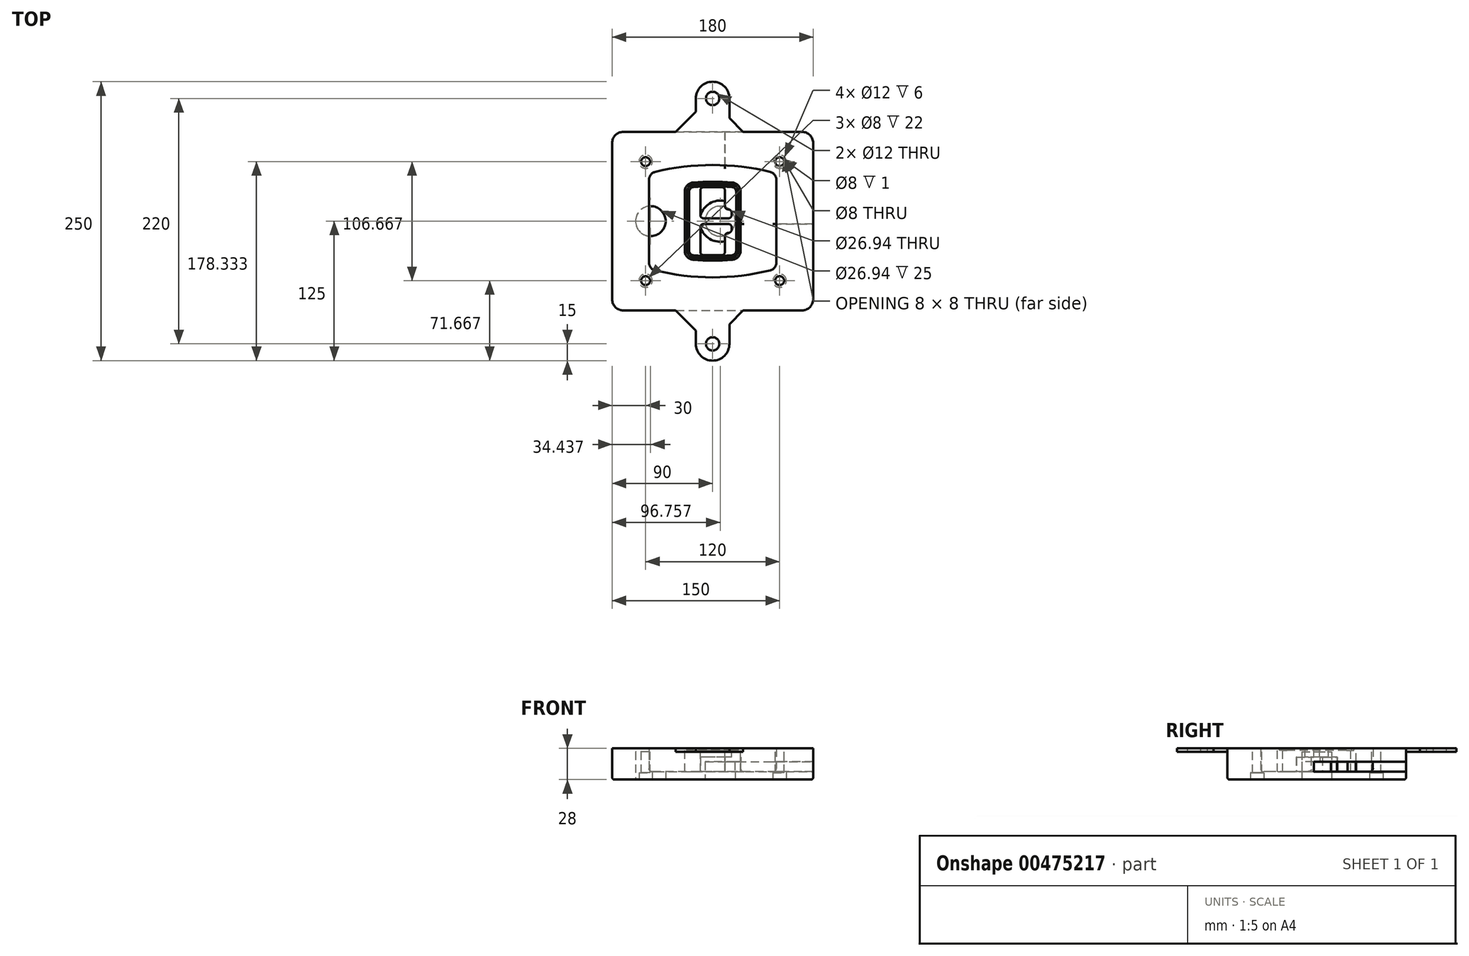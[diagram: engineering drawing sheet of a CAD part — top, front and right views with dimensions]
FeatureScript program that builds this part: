
annotation { "Feature Type Name" : "Feature", "Feature Type Description" : "" }
export const myFeature = defineFeature(function(context is Context, id is Id, definition is map)
    precondition{}
    {
        {
            var Q0;
            Q0=qCreatedBy(makeId("Top.planeOp"),FACE);
            var sketch = newSketch(context, id + "F0", { "sketchPlane" : qUnion([Q0])});
            skPoint(sketch, "E0.rect.middle", {"position": v(0, 0) * mm});
            skLineSegment(sketch, "E1.bottom", {"start": v(-80, -80) * mm, "end": v(80, -80) * mm});
            skLineSegment(sketch, "E1.top", {"start": v(-80, 80) * mm, "end": v(80, 80) * mm});
            skLineSegment(sketch, "E1.left", {"start": v(-90, -70) * mm, "end": v(-90, 70) * mm});
            skLineSegment(sketch, "E1.right", {"start": v(90, -70) * mm, "end": v(90, 70) * mm});
            skLineSegment(sketch, "E2", {"start": v(-90, 80) * mm, "end": v(90, -80) * mm, "construction": true});
            skLineSegment(sketch, "E3", {"start": v(90, 80) * mm, "end": v(-90, -80) * mm, "construction": true});
            skCircle(sketch, "E4", {"center": v(-60, 53.33) * mm, "radius": 4 * mm});
            skCircle(sketch, "E5", {"center": v(60, 53.33) * mm, "radius": 4 * mm});
            skCircle(sketch, "E6", {"center": v(60, -53.33) * mm, "radius": 4 * mm});
            skCircle(sketch, "E7", {"center": v(-60, -53.33) * mm, "radius": 4 * mm});
            skLineSegment(sketch, "E8", {"start": v(-60, 53.33) * mm, "end": v(60, 53.33) * mm, "construction": true});
            skLineSegment(sketch, "E9", {"start": v(60, 53.33) * mm, "end": v(60, -53.33) * mm, "construction": true});
            skLineSegment(sketch, "E10", {"start": v(60, -53.33) * mm, "end": v(-60, -53.33) * mm, "construction": true});
            skLineSegment(sketch, "E11", {"start": v(-60, -53.33) * mm, "end": v(-60, 53.33) * mm, "construction": true});
            skLineSegment(sketch, "E12", {"start": v(-60, 37.3) * mm, "end": v(-60, -37.3) * mm});
            skLineSegment(sketch, "E13", {"start": v(60, 37.3) * mm, "end": v(60, -37.3) * mm});
            skArc(sketch, "E14", {"start": v(52.38, 47.01) * mm, "mid": v(0, 53.33) * mm, "end": v(-52.38, 47.01) * mm});
            skArc(sketch, "E15", {"start": v(-52.38, -47.01) * mm, "mid": v(0, -53.33) * mm, "end": v(52.38, -47.01) * mm});
            skLineSegment(sketch, "E16", {"start": v(-60, 0) * mm, "end": v(60, 0) * mm, "construction": true});
            skPoint(sketch, "E17.visualSharp", {"position": v(-60, -45) * mm});
            skArc(sketch, "E17.filletArc", {"start": v(-60, -37.3) * mm, "mid": v(-57.87, -43.47) * mm, "end": v(-52.38, -47.01) * mm});
            skPoint(sketch, "E18.visualSharp", {"position": v(-60, 45) * mm});
            skArc(sketch, "E18.filletArc", {"start": v(-52.38, 47.01) * mm, "mid": v(-57.87, 43.47) * mm, "end": v(-60, 37.3) * mm});
            skPoint(sketch, "E19.visualSharp", {"position": v(60, 45) * mm});
            skArc(sketch, "E19.filletArc", {"start": v(60, 37.3) * mm, "mid": v(57.87, 43.47) * mm, "end": v(52.38, 47.01) * mm});
            skPoint(sketch, "E20.visualSharp", {"position": v(60, -45) * mm});
            skArc(sketch, "E20.filletArc", {"start": v(52.38, -47.01) * mm, "mid": v(57.87, -43.47) * mm, "end": v(60, -37.3) * mm});
            skPoint(sketch, "E21.visualSharp", {"position": v(-90, 80) * mm});
            skArc(sketch, "E21.filletArc", {"start": v(-80, 80) * mm, "mid": v(-87.07, 77.07) * mm, "end": v(-90, 70) * mm});
            skPoint(sketch, "E22.visualSharp", {"position": v(90, 80) * mm});
            skArc(sketch, "E22.filletArc", {"start": v(90, 70) * mm, "mid": v(87.07, 77.07) * mm, "end": v(80, 80) * mm});
            skPoint(sketch, "E23.visualSharp", {"position": v(90, -80) * mm});
            skArc(sketch, "E23.filletArc", {"start": v(80, -80) * mm, "mid": v(87.07, -77.07) * mm, "end": v(90, -70) * mm});
            skPoint(sketch, "E24.visualSharp", {"position": v(-90, -80) * mm});
            skArc(sketch, "E24.filletArc", {"start": v(-90, -70) * mm, "mid": v(-87.07, -77.07) * mm, "end": v(-80, -80) * mm});
            skArc(sketch, "E25.0", {"start": v(57, 37.3) * mm, "mid": v(55.5, 41.62) * mm, "end": v(51.67, 44.1) * mm});
            skLineSegment(sketch, "E25.1", {"start": v(57, 37.3) * mm, "end": v(57, -37.3) * mm});
            skArc(sketch, "E25.2", {"start": v(51.67, -44.1) * mm, "mid": v(55.5, -41.62) * mm, "end": v(57, -37.3) * mm});
            skArc(sketch, "E25.3", {"start": v(-51.67, -44.1) * mm, "mid": v(0, -50.33) * mm, "end": v(51.67, -44.1) * mm});
            skArc(sketch, "E25.4", {"start": v(-57, -37.3) * mm, "mid": v(-55.5, -41.62) * mm, "end": v(-51.67, -44.1) * mm});
            skArc(sketch, "E25.5", {"start": v(51.67, 44.1) * mm, "mid": v(0, 50.33) * mm, "end": v(-51.67, 44.1) * mm});
            skLineSegment(sketch, "E25.6", {"start": v(-57, 37.3) * mm, "end": v(-57, -37.3) * mm});
            skArc(sketch, "E25.7", {"start": v(-51.67, 44.1) * mm, "mid": v(-55.5, 41.62) * mm, "end": v(-57, 37.3) * mm});
            skArc(sketch, "E26.0", {"start": v(-53.33, 50.9) * mm, "mid": v(-61.01, 45.94) * mm, "end": v(-64, 37.3) * mm});
            skArc(sketch, "E26.1", {"start": v(53.33, 50.9) * mm, "mid": v(0, 57.33) * mm, "end": v(-53.33, 50.9) * mm});
            skArc(sketch, "E26.2", {"start": v(64, 37.3) * mm, "mid": v(61.01, 45.94) * mm, "end": v(53.33, 50.9) * mm});
            skLineSegment(sketch, "E26.3", {"start": v(64, 37.3) * mm, "end": v(64, -37.3) * mm});
            skArc(sketch, "E26.4", {"start": v(53.33, -50.9) * mm, "mid": v(61.01, -45.94) * mm, "end": v(64, -37.3) * mm});
            skLineSegment(sketch, "E26.5", {"start": v(-64, 37.3) * mm, "end": v(-64, -37.3) * mm});
            skArc(sketch, "E26.6", {"start": v(-53.33, -50.9) * mm, "mid": v(0, -57.33) * mm, "end": v(53.33, -50.9) * mm});
            skArc(sketch, "E26.7", {"start": v(-64, -37.3) * mm, "mid": v(-61.01, -45.94) * mm, "end": v(-53.33, -50.9) * mm});
            skSolve(sketch);
        }
        {
            var Q0;
            Q0=makeQuery(id+"F0.imprint","IMPRINT",FACE,{"disambiguationData":[TD([[makeQuery(id+"F0.imprint","IMPRINT",EDGE,{"derivedFrom":sQuery(id+"F0.wireOp",EDGE,"E1.bottom")}),1.0]])]});
            var Q1;
            Q1=makeQuery(id+"F0.imprint","IMPRINT",FACE,{"disambiguationData":[TD([[makeQuery(id+"F0.imprint","IMPRINT",EDGE,{"derivedFrom":sQuery(id+"F0.wireOp",EDGE,"E12")}),1.0]])]});
            var Q2;
            Q2=makeQuery(id+"F0.imprint","IMPRINT",FACE,{"disambiguationData":[TD([[makeQuery(id+"F0.imprint","IMPRINT",EDGE,{"derivedFrom":sQuery(id+"F0.wireOp",EDGE,"E25.0")}),1.0]])]});
            var Q3;
            Q3=makeQuery(id+"F0.imprint","IMPRINT",FACE,{"disambiguationData":[TD([[makeQuery(id+"F0.imprint","IMPRINT",EDGE,{"derivedFrom":sQuery(id+"F0.wireOp",EDGE,"E12")}),-1.0]])]});
            extrude(context, id + "F1", {"entities" : qUnion([Q0, Q1, Q2, Q3]), "oppositeDirection" : true, "depth" : 25 * mm});
        }
        {
            var Q0;
            Q0=makeQuery(id+"F0.imprint","IMPRINT",FACE,{"disambiguationData":[TD([[makeQuery(id+"F0.imprint","IMPRINT",EDGE,{"derivedFrom":sQuery(id+"F0.wireOp",EDGE,"E12")}),1.0]])]});
            extrude(context, id + "F2", {"entities" : qUnion([Q0]), "operationType" : NewBodyOperationType.ADD, "depth" : 3 * mm});
        }
        {
            var Q0;
            Q0=makeQuery(id+"F0.imprint","IMPRINT",FACE,{"disambiguationData":[TD([[makeQuery(id+"F0.imprint","IMPRINT",EDGE,{"derivedFrom":sQuery(id+"F0.wireOp",EDGE,"E25.0")}),1.0]])]});
            extrude(context, id + "F3", {"entities" : qUnion([Q0]), "operationType" : NewBodyOperationType.REMOVE, "oppositeDirection" : true, "depth" : 18 * mm});
        }
        {
            var Q0;
            Q0=makeQuery(id+"F2.opExtrude","CAP_FACE",FACE,{"disambiguationData":[OSD([sQuery(id+"F0.wireOp",EDGE,"E12"),sQuery(id+"F0.wireOp",EDGE,"E13"),sQuery(id+"F0.wireOp",EDGE,"E14"),sQuery(id+"F0.wireOp",EDGE,"E15"),sQuery(id+"F0.wireOp",EDGE,"E17.filletArc"),sQuery(id+"F0.wireOp",EDGE,"E18.filletArc"),sQuery(id+"F0.wireOp",EDGE,"E19.filletArc"),sQuery(id+"F0.wireOp",EDGE,"E20.filletArc"),sQuery(id+"F0.wireOp",EDGE,"E25.0"),sQuery(id+"F0.wireOp",EDGE,"E25.1"),sQuery(id+"F0.wireOp",EDGE,"E25.2"),sQuery(id+"F0.wireOp",EDGE,"E25.3"),sQuery(id+"F0.wireOp",EDGE,"E25.4"),sQuery(id+"F0.wireOp",EDGE,"E25.5"),sQuery(id+"F0.wireOp",EDGE,"E25.6"),sQuery(id+"F0.wireOp",EDGE,"E25.7")])],"isStart":false});
            var sketch = newSketch(context, id + "F4", { "sketchPlane" : qUnion([Q0])});
            skArc(sketch, "E27.0", {"start": v(-17.7, -34.56) * mm, "mid": v(0, -35.33) * mm, "end": v(17.7, -34.56) * mm});
            skArc(sketch, "E28.0", {"start": v(17.7, 34.56) * mm, "mid": v(0, 35.33) * mm, "end": v(-17.7, 34.56) * mm});
            skLineSegment(sketch, "E29", {"start": v(-25, 26.59) * mm, "end": v(-25, -26.59) * mm});
            skLineSegment(sketch, "E30", {"start": v(25, 26.59) * mm, "end": v(25, -26.59) * mm});
            skLineSegment(sketch, "E31", {"start": v(-25, 33.78) * mm, "end": v(25, 33.78) * mm, "construction": true});
            skLineSegment(sketch, "E32", {"start": v(-25, -33.78) * mm, "end": v(25, -33.78) * mm, "construction": true});
            skPoint(sketch, "E33.visualSharp", {"position": v(-25, 33.78) * mm});
            skArc(sketch, "E33.filletArc", {"start": v(-17.7, 34.56) * mm, "mid": v(-22.9, 32) * mm, "end": v(-25, 26.59) * mm});
            skPoint(sketch, "E34.visualSharp", {"position": v(25, 33.78) * mm});
            skArc(sketch, "E34.filletArc", {"start": v(25, 26.59) * mm, "mid": v(22.9, 32) * mm, "end": v(17.7, 34.56) * mm});
            skPoint(sketch, "E35.visualSharp", {"position": v(25, -33.78) * mm});
            skArc(sketch, "E35.filletArc", {"start": v(17.7, -34.56) * mm, "mid": v(22.9, -32) * mm, "end": v(25, -26.59) * mm});
            skPoint(sketch, "E36.visualSharp", {"position": v(-25, -33.78) * mm});
            skArc(sketch, "E36.filletArc", {"start": v(-25, -26.59) * mm, "mid": v(-22.9, -32) * mm, "end": v(-17.7, -34.56) * mm});
            skArc(sketch, "E37.0", {"start": v(51.67, 44.1) * mm, "mid": v(0, 50.33) * mm, "end": v(-51.67, 44.1) * mm});
            skArc(sketch, "E37.1", {"start": v(-51.67, 44.1) * mm, "mid": v(-55.5, 41.62) * mm, "end": v(-57, 37.3) * mm});
            skLineSegment(sketch, "E37.2", {"start": v(-57, 37.3) * mm, "end": v(-57, -37.3) * mm});
            skArc(sketch, "E37.3", {"start": v(-57, -37.3) * mm, "mid": v(-55.5, -41.62) * mm, "end": v(-51.67, -44.1) * mm});
            skArc(sketch, "E37.4", {"start": v(-51.67, -44.1) * mm, "mid": v(0, -50.33) * mm, "end": v(51.67, -44.1) * mm});
            skArc(sketch, "E37.5", {"start": v(51.67, -44.1) * mm, "mid": v(55.5, -41.62) * mm, "end": v(57, -37.3) * mm});
            skLineSegment(sketch, "E37.6", {"start": v(57, 37.3) * mm, "end": v(57, -37.3) * mm});
            skArc(sketch, "E37.7", {"start": v(57, 37.3) * mm, "mid": v(55.5, 41.62) * mm, "end": v(51.67, 44.1) * mm});
            skLineSegment(sketch, "E38.0", {"start": v(23, 26.59) * mm, "end": v(23, -26.59) * mm});
            skArc(sketch, "E38.1", {"start": v(17.53, -32.56) * mm, "mid": v(21.42, -30.64) * mm, "end": v(23, -26.59) * mm});
            skArc(sketch, "E38.2", {"start": v(-17.53, -32.56) * mm, "mid": v(0, -33.33) * mm, "end": v(17.53, -32.56) * mm});
            skArc(sketch, "E38.3", {"start": v(-23, -26.59) * mm, "mid": v(-21.42, -30.64) * mm, "end": v(-17.53, -32.56) * mm});
            skLineSegment(sketch, "E38.4", {"start": v(-23, 26.59) * mm, "end": v(-23, -26.59) * mm});
            skArc(sketch, "E38.5", {"start": v(23, 26.59) * mm, "mid": v(21.42, 30.64) * mm, "end": v(17.53, 32.56) * mm});
            skArc(sketch, "E38.6", {"start": v(-17.53, 32.56) * mm, "mid": v(-21.42, 30.64) * mm, "end": v(-23, 26.59) * mm});
            skArc(sketch, "E38.7", {"start": v(17.53, 32.56) * mm, "mid": v(0, 33.33) * mm, "end": v(-17.53, 32.56) * mm});
            skArc(sketch, "E39.0", {"start": v(21, 26.59) * mm, "mid": v(19.95, 29.29) * mm, "end": v(17.35, 30.57) * mm});
            skLineSegment(sketch, "E39.1", {"start": v(21, 26.59) * mm, "end": v(21, -26.59) * mm});
            skArc(sketch, "E39.2", {"start": v(17.35, -30.57) * mm, "mid": v(19.95, -29.29) * mm, "end": v(21, -26.59) * mm});
            skArc(sketch, "E39.3", {"start": v(-17.35, -30.57) * mm, "mid": v(0, -31.33) * mm, "end": v(17.35, -30.57) * mm});
            skArc(sketch, "E39.4", {"start": v(-21, -26.59) * mm, "mid": v(-19.95, -29.29) * mm, "end": v(-17.35, -30.57) * mm});
            skArc(sketch, "E39.5", {"start": v(17.35, 30.57) * mm, "mid": v(0, 31.33) * mm, "end": v(-17.35, 30.57) * mm});
            skLineSegment(sketch, "E39.6", {"start": v(-21, 26.59) * mm, "end": v(-21, -26.59) * mm});
            skArc(sketch, "E39.7", {"start": v(-17.35, 30.57) * mm, "mid": v(-19.95, 29.29) * mm, "end": v(-21, 26.59) * mm});
            skLineSegment(sketch, "E40", {"start": v(-25, 0) * mm, "end": v(25, 0) * mm, "construction": true});
            skLineSegment(sketch, "E41", {"start": v(-11, 5.5) * mm, "end": v(-11, 27.5) * mm});
            skLineSegment(sketch, "E42", {"start": v(-8, 30.5) * mm, "end": v(8, 30.5) * mm});
            skLineSegment(sketch, "E43", {"start": v(11, 27.5) * mm, "end": v(11, 13.5) * mm});
            skLineSegment(sketch, "E44", {"start": v(14, 10.5) * mm, "end": v(14, 10.5) * mm});
            skLineSegment(sketch, "E45", {"start": v(17, 7.5) * mm, "end": v(17, 5.5) * mm});
            skLineSegment(sketch, "E46", {"start": v(14, 2.5) * mm, "end": v(-8, 2.5) * mm});
            skPoint(sketch, "E47.visualSharp", {"position": v(-11, 30.5) * mm});
            skArc(sketch, "E47.filletArc", {"start": v(-8, 30.5) * mm, "mid": v(-10.12, 29.62) * mm, "end": v(-11, 27.5) * mm});
            skPoint(sketch, "E48.visualSharp", {"position": v(11, 30.5) * mm});
            skArc(sketch, "E48.filletArc", {"start": v(11, 27.5) * mm, "mid": v(10.12, 29.62) * mm, "end": v(8, 30.5) * mm});
            skPoint(sketch, "E49.visualSharp", {"position": v(11, 10.5) * mm});
            skArc(sketch, "E49.filletArc", {"start": v(11, 13.5) * mm, "mid": v(11.88, 11.38) * mm, "end": v(14, 10.5) * mm});
            skPoint(sketch, "E50.visualSharp", {"position": v(17, 10.5) * mm});
            skArc(sketch, "E50.filletArc", {"start": v(17, 7.5) * mm, "mid": v(16.12, 9.62) * mm, "end": v(14, 10.5) * mm});
            skPoint(sketch, "E51.visualSharp", {"position": v(17, 2.5) * mm});
            skArc(sketch, "E51.filletArc", {"start": v(14, 2.5) * mm, "mid": v(16.12, 3.38) * mm, "end": v(17, 5.5) * mm});
            skPoint(sketch, "E52.visualSharp", {"position": v(-11, 2.5) * mm});
            skArc(sketch, "E52.filletArc", {"start": v(-11, 5.5) * mm, "mid": v(-10.12, 3.38) * mm, "end": v(-8, 2.5) * mm});
            skLineSegment(sketch, "E53.0.MirrorCS", {"start": v(14, -2.5) * mm, "end": v(-8, -2.5) * mm});
            skArc(sketch, "E54.0.MirrorCS", {"start": v(-11, -5.5) * mm, "mid": v(-10.12, -3.38) * mm, "end": v(-8, -2.5) * mm});
            skLineSegment(sketch, "E55.0.MirrorCS", {"start": v(-11, -5.5) * mm, "end": v(-11, -27.5) * mm});
            skArc(sketch, "E56.0.MirrorCS", {"start": v(-8, -30.5) * mm, "mid": v(-10.12, -29.62) * mm, "end": v(-11, -27.5) * mm});
            skLineSegment(sketch, "E57.0.MirrorCS", {"start": v(-8, -30.5) * mm, "end": v(8, -30.5) * mm});
            skArc(sketch, "E58.0.MirrorCS", {"start": v(11, -27.5) * mm, "mid": v(10.12, -29.62) * mm, "end": v(8, -30.5) * mm});
            skLineSegment(sketch, "E59.0.MirrorCS", {"start": v(11, -27.5) * mm, "end": v(11, -13.5) * mm});
            skArc(sketch, "E60.0.MirrorCS", {"start": v(11, -13.5) * mm, "mid": v(11.88, -11.38) * mm, "end": v(14, -10.5) * mm});
            skArc(sketch, "E61.0.MirrorCS", {"start": v(17, -7.5) * mm, "mid": v(16.12, -9.62) * mm, "end": v(14, -10.5) * mm});
            skLineSegment(sketch, "E62.0.MirrorCS", {"start": v(17, -7.5) * mm, "end": v(17, -5.5) * mm});
            skArc(sketch, "E63.0.MirrorCS", {"start": v(14, -2.5) * mm, "mid": v(16.12, -3.38) * mm, "end": v(17, -5.5) * mm});
            skSolve(sketch);
        }
        {
            var Q0;
            Q0=makeQuery(id+"F4.imprint","IMPRINT",FACE,{"disambiguationData":[TD([[makeQuery(id+"F4.imprint","IMPRINT",EDGE,{"derivedFrom":sQuery(id+"F4.wireOp",EDGE,"E27.0")}),1.0]])]});
            var Q1;
            Q1=makeQuery(id+"F4.imprint","IMPRINT",FACE,{"disambiguationData":[TD([[makeQuery(id+"F4.imprint","IMPRINT",EDGE,{"derivedFrom":sQuery(id+"F4.wireOp",EDGE,"E38.0")}),-1.0]])]});
            var Q2;
            Q2=makeQuery(id+"F4.imprint","IMPRINT",FACE,{"disambiguationData":[TD([[makeQuery(id+"F4.imprint","IMPRINT",EDGE,{"derivedFrom":sQuery(id+"F4.wireOp",EDGE,"E39.0")}),1.0]])]});
            extrude(context, id + "F5", {"entities" : qUnion([Q0, Q1, Q2]), "operationType" : NewBodyOperationType.ADD, "endBound" : BoundingType.UP_TO_NEXT, "oppositeDirection" : true, "depth" : 25 * mm});
        }
        {
            var Q0;
            Q0=makeQuery(id+"F4.imprint","IMPRINT",FACE,{"disambiguationData":[TD([[makeQuery(id+"F4.imprint","IMPRINT",EDGE,{"derivedFrom":sQuery(id+"F4.wireOp",EDGE,"E38.0")}),-1.0]])]});
            extrude(context, id + "F6", {"entities" : qUnion([Q0]), "operationType" : NewBodyOperationType.REMOVE, "oppositeDirection" : true, "depth" : 2 * mm});
        }
        {
            var Q0;
            Q0=makeQuery(id+"F1.opExtrude","CAP_FACE",FACE,{"disambiguationData":[OSD([sQuery(id+"F0.wireOp",EDGE,"E1.bottom"),sQuery(id+"F0.wireOp",EDGE,"E1.top"),sQuery(id+"F0.wireOp",EDGE,"E1.left"),sQuery(id+"F0.wireOp",EDGE,"E1.right"),sQuery(id+"F0.wireOp",EDGE,"E4"),sQuery(id+"F0.wireOp",EDGE,"E5"),sQuery(id+"F0.wireOp",EDGE,"E6"),sQuery(id+"F0.wireOp",EDGE,"E7"),sQuery(id+"F0.wireOp",EDGE,"E21.filletArc"),sQuery(id+"F0.wireOp",EDGE,"E22.filletArc"),sQuery(id+"F0.wireOp",EDGE,"E23.filletArc"),sQuery(id+"F0.wireOp",EDGE,"E24.filletArc")])],"isStart":false});
            var sketch = newSketch(context, id + "F7", { "sketchPlane" : qUnion([Q0])});
            skCircle(sketch, "E64", {"center": v(6.76, 0) * mm, "radius": 13.47 * mm});
            skCircle(sketch, "E65", {"center": v(-55.56, 0) * mm, "radius": 13.47 * mm});
            skLineSegment(sketch, "E66", {"start": v(90, 0) * mm, "end": v(-90, 0) * mm});
            skCircle(sketch, "E67", {"center": v(6.76, 0) * mm, "radius": 18.47 * mm});
            skCircle(sketch, "E68", {"center": v(60, -53.33) * mm, "radius": 6 * mm});
            skCircle(sketch, "E69", {"center": v(-60, -53.33) * mm, "radius": 6 * mm});
            skCircle(sketch, "E70", {"center": v(-60, 53.33) * mm, "radius": 6 * mm});
            skCircle(sketch, "E71", {"center": v(60, 53.33) * mm, "radius": 6 * mm});
            skSolve(sketch);
        }
        {
            var Q0;
            {var subQ1=sQuery(id+"F7.wireOp",EDGE,"E66");var subQ4=sQuery(id+"F7.wireOp",EDGE,"E64");var subQ6=makeQuery(id+"F7.imprint","INTERSECT",VERTEX,{"disambiguationData":[OD(0.0)],"derivedFrom":[subQ4,subQ1]});Q0=makeQuery(id+"F7.imprint","IMPRINT",FACE,{"disambiguationData":[TD([[makeQuery(id+"F7.imprint","IMPRINT",EDGE,{"disambiguationData":[TD([[subQ6,-1.0]])],"derivedFrom":subQ4}),-1.0]])]});}
            var Q1;
            {var subQ0=sQuery(id+"F7.wireOp",EDGE,"E66");var subQ1=sQuery(id+"F7.wireOp",EDGE,"E64");var subQ3=makeQuery(id+"F7.imprint","INTERSECT",VERTEX,{"disambiguationData":[OD(0.0)],"derivedFrom":[subQ1,subQ0]});Q1=makeQuery(id+"F7.imprint","IMPRINT",FACE,{"disambiguationData":[TD([[makeQuery(id+"F7.imprint","IMPRINT",EDGE,{"disambiguationData":[TD([[subQ3,-1.0]])],"derivedFrom":subQ1}),1.0]])]});}
            var Q2;
            {var subQ0=sQuery(id+"F7.wireOp",EDGE,"E66");var subQ1=sQuery(id+"F7.wireOp",EDGE,"E64");var subQ3=makeQuery(id+"F7.imprint","INTERSECT",VERTEX,{"disambiguationData":[OD(0.0)],"derivedFrom":[subQ1,subQ0]});Q2=makeQuery(id+"F7.imprint","IMPRINT",FACE,{"disambiguationData":[TD([[makeQuery(id+"F7.imprint","IMPRINT",EDGE,{"disambiguationData":[TD([[subQ3,1.0]])],"derivedFrom":subQ1}),1.0]])]});}
            var Q3;
            {var subQ1=sQuery(id+"F7.wireOp",EDGE,"E66");var subQ4=sQuery(id+"F7.wireOp",EDGE,"E64");var subQ6=makeQuery(id+"F7.imprint","INTERSECT",VERTEX,{"disambiguationData":[OD(0.0)],"derivedFrom":[subQ4,subQ1]});Q3=makeQuery(id+"F7.imprint","IMPRINT",FACE,{"disambiguationData":[TD([[makeQuery(id+"F7.imprint","IMPRINT",EDGE,{"disambiguationData":[TD([[subQ6,1.0]])],"derivedFrom":subQ4}),-1.0]])]});}
            extrude(context, id + "F8", {"entities" : qUnion([Q0, Q1, Q2, Q3]), "operationType" : NewBodyOperationType.ADD, "oppositeDirection" : true, "depth" : 20 * mm});
        }
        {
            var Q0;
            {var subQ0=sQuery(id+"F7.wireOp",EDGE,"E66");var subQ1=sQuery(id+"F7.wireOp",EDGE,"E64");var subQ3=makeQuery(id+"F7.imprint","INTERSECT",VERTEX,{"disambiguationData":[OD(0.0)],"derivedFrom":[subQ1,subQ0]});Q0=makeQuery(id+"F7.imprint","IMPRINT",FACE,{"disambiguationData":[TD([[makeQuery(id+"F7.imprint","IMPRINT",EDGE,{"disambiguationData":[TD([[subQ3,-1.0]])],"derivedFrom":subQ1}),1.0]])]});}
            var Q1;
            {var subQ0=sQuery(id+"F7.wireOp",EDGE,"E66");var subQ1=sQuery(id+"F7.wireOp",EDGE,"E64");var subQ3=makeQuery(id+"F7.imprint","INTERSECT",VERTEX,{"disambiguationData":[OD(0.0)],"derivedFrom":[subQ1,subQ0]});Q1=makeQuery(id+"F7.imprint","IMPRINT",FACE,{"disambiguationData":[TD([[makeQuery(id+"F7.imprint","IMPRINT",EDGE,{"disambiguationData":[TD([[subQ3,1.0]])],"derivedFrom":subQ1}),1.0]])]});}
            extrude(context, id + "F9", {"entities" : qUnion([Q0, Q1]), "operationType" : NewBodyOperationType.REMOVE, "oppositeDirection" : true, "depth" : 16 * mm});
        }
        {
            var Q0;
            {var subQ0=sQuery(id+"F7.wireOp",EDGE,"E66");var subQ1=sQuery(id+"F7.wireOp",EDGE,"E65");var subQ3=makeQuery(id+"F7.imprint","INTERSECT",VERTEX,{"disambiguationData":[OD(0.0)],"derivedFrom":[subQ1,subQ0]});Q0=makeQuery(id+"F7.imprint","IMPRINT",FACE,{"disambiguationData":[TD([[makeQuery(id+"F7.imprint","IMPRINT",EDGE,{"disambiguationData":[TD([[subQ3,-1.0]])],"derivedFrom":subQ1}),1.0]])]});}
            var Q1;
            {var subQ0=sQuery(id+"F7.wireOp",EDGE,"E66");var subQ1=sQuery(id+"F7.wireOp",EDGE,"E65");var subQ3=makeQuery(id+"F7.imprint","INTERSECT",VERTEX,{"disambiguationData":[OD(0.0)],"derivedFrom":[subQ1,subQ0]});Q1=makeQuery(id+"F7.imprint","IMPRINT",FACE,{"disambiguationData":[TD([[makeQuery(id+"F7.imprint","IMPRINT",EDGE,{"disambiguationData":[TD([[subQ3,1.0]])],"derivedFrom":subQ1}),1.0]])]});}
            extrude(context, id + "F10", {"entities" : qUnion([Q0, Q1]), "operationType" : NewBodyOperationType.REMOVE, "oppositeDirection" : true, "depth" : 25 * mm});
        }
        {
            var Q0;
            Q0=makeQuery(id+"F7.imprint","IMPRINT",FACE,{"disambiguationData":[TD([[makeQuery(id+"F7.imprint","IMPRINT",EDGE,{"derivedFrom":sQuery(id+"F7.wireOp",EDGE,"E68")}),1.0]])]});
            var Q1;
            Q1=makeQuery(id+"F7.imprint","IMPRINT",FACE,{"disambiguationData":[TD([[makeQuery(id+"F7.imprint","IMPRINT",EDGE,{"derivedFrom":makeQuery(id+"F1.opExtrude","CAP_EDGE",EDGE,{"disambiguationData":[OSD([sQuery(id+"F0.wireOp",EDGE,"E5")])],"isStart":false})}),-1.0]])]});
            var Q2;
            Q2=makeQuery(id+"F7.imprint","IMPRINT",FACE,{"disambiguationData":[TD([[makeQuery(id+"F7.imprint","IMPRINT",EDGE,{"derivedFrom":sQuery(id+"F7.wireOp",EDGE,"E69")}),1.0]])]});
            var Q3;
            Q3=makeQuery(id+"F7.imprint","IMPRINT",FACE,{"disambiguationData":[TD([[makeQuery(id+"F7.imprint","IMPRINT",EDGE,{"derivedFrom":makeQuery(id+"F1.opExtrude","CAP_EDGE",EDGE,{"disambiguationData":[OSD([sQuery(id+"F0.wireOp",EDGE,"E4")])],"isStart":false})}),-1.0]])]});
            var Q4;
            Q4=makeQuery(id+"F7.imprint","IMPRINT",FACE,{"disambiguationData":[TD([[makeQuery(id+"F7.imprint","IMPRINT",EDGE,{"derivedFrom":sQuery(id+"F7.wireOp",EDGE,"E70")}),1.0]])]});
            var Q5;
            Q5=makeQuery(id+"F7.imprint","IMPRINT",FACE,{"disambiguationData":[TD([[makeQuery(id+"F7.imprint","IMPRINT",EDGE,{"derivedFrom":makeQuery(id+"F1.opExtrude","CAP_EDGE",EDGE,{"disambiguationData":[OSD([sQuery(id+"F0.wireOp",EDGE,"E7")])],"isStart":false})}),-1.0]])]});
            var Q6;
            Q6=makeQuery(id+"F7.imprint","IMPRINT",FACE,{"disambiguationData":[TD([[makeQuery(id+"F7.imprint","IMPRINT",EDGE,{"derivedFrom":sQuery(id+"F7.wireOp",EDGE,"E71")}),1.0]])]});
            var Q7;
            Q7=makeQuery(id+"F7.imprint","IMPRINT",FACE,{"disambiguationData":[TD([[makeQuery(id+"F7.imprint","IMPRINT",EDGE,{"derivedFrom":makeQuery(id+"F1.opExtrude","CAP_EDGE",EDGE,{"disambiguationData":[OSD([sQuery(id+"F0.wireOp",EDGE,"E6")])],"isStart":false})}),-1.0]])]});
            extrude(context, id + "F11", {"entities" : qUnion([Q0, Q1, Q2, Q3, Q4, Q5, Q6, Q7]), "operationType" : NewBodyOperationType.REMOVE, "oppositeDirection" : true, "depth" : 6 * mm});
        }
        {
            var Q0;
            Q0=makeQuery(id+"F9.boolean.opBoolean","COPY",FACE,{"derivedFrom":makeQuery(id+"F9.opExtrude","CAP_FACE",FACE,{"disambiguationData":[OSD([sQuery(id+"F7.wireOp",EDGE,"E64")])],"isStart":false})});
            var sketch = newSketch(context, id + "F12", { "sketchPlane" : qUnion([Q0])});
            skArc(sketch, "E72.0", {"start": v(11, -88.19) * mm, "mid": v(97.1, -83.6) * mm, "end": v(92.5, 2.5) * mm});
            skLineSegment(sketch, "E72.1", {"start": v(11, -17.97) * mm, "end": v(11, -17.97) * mm});
            skLineSegment(sketch, "E73", {"start": v(92.5, -105.13) * mm, "end": v(102.3, -105.13) * mm});
            skLineSegment(sketch, "E74.0", {"start": v(92.5, 2.5) * mm, "end": v(14, 2.5) * mm});
            skArc(sketch, "E74.1", {"start": v(14, 2.5) * mm, "mid": v(16.12, 3.38) * mm, "end": v(17, 5.5) * mm});
            skLineSegment(sketch, "E74.2", {"start": v(17, 7.5) * mm, "end": v(17, 5.5) * mm});
            skArc(sketch, "E74.3", {"start": v(17, 7.5) * mm, "mid": v(16.12, 9.62) * mm, "end": v(14, 10.5) * mm});
            skArc(sketch, "E74.4", {"start": v(11, 13.5) * mm, "mid": v(11.88, 11.38) * mm, "end": v(14, 10.5) * mm});
            skLineSegment(sketch, "E74.5", {"start": v(11, 13.5) * mm, "end": v(11, -88.19) * mm});
            skLineSegment(sketch, "E74.7", {"start": v(92.5, -2.5) * mm, "end": v(14, -2.5) * mm});
            skArc(sketch, "E74.8", {"start": v(14, -2.5) * mm, "mid": v(16.12, -3.38) * mm, "end": v(17, -5.5) * mm});
            skLineSegment(sketch, "E74.9", {"start": v(17, -7.5) * mm, "end": v(17, -5.5) * mm});
            skArc(sketch, "E74.10", {"start": v(17, -7.5) * mm, "mid": v(16.12, -9.62) * mm, "end": v(14, -10.5) * mm});
            skArc(sketch, "E74.11", {"start": v(11, -13.5) * mm, "mid": v(11.88, -11.38) * mm, "end": v(14, -10.5) * mm});
            skLineSegment(sketch, "E74.12", {"start": v(11, -17.97) * mm, "end": v(11, -13.5) * mm});
            skPoint(sketch, "E75.orphan", {"position": v(11, -27.5) * mm});
            skPoint(sketch, "E76.orphan", {"position": v(-8, -2.5) * mm});
            skPoint(sketch, "E77.orphan", {"position": v(-8, 2.5) * mm});
            skPoint(sketch, "E78.orphan", {"position": v(11, 27.5) * mm});
            skSolve(sketch);
        }
        {
            var Q0;
            {var subQ7=sQuery(id+"F12.wireOp",EDGE,"E72.0");var subQ14=sQuery(id+"F12.wireOp",EDGE,"E72.1");var subQ16=sQuery(id+"F12.wireOp",EDGE,"E74.1");var subQ18=sQuery(id+"F12.wireOp",EDGE,"E74.8");Q0=qUnion([makeQuery(id+"F12.imprint","IMPRINT",FACE,{"disambiguationData":[TD([[makeQuery(id+"F12.imprint","IMPRINT",EDGE,{"derivedFrom":subQ7}),1.0]])]}),makeQuery(id+"F12.imprint","IMPRINT",FACE,{"disambiguationData":[TD([[makeQuery(id+"F12.imprint","IMPRINT",EDGE,{"derivedFrom":subQ14}),1.0]])]}),makeQuery(id+"F12.imprint","IMPRINT",FACE,{"disambiguationData":[TD([[makeQuery(id+"F12.imprint","IMPRINT",EDGE,{"derivedFrom":subQ16}),1.0]])]}),makeQuery(id+"F12.imprint","IMPRINT",FACE,{"disambiguationData":[TD([[makeQuery(id+"F12.imprint","IMPRINT",EDGE,{"derivedFrom":subQ18}),-1.0]])]})]);}
            var Q1;
            Q1=makeQuery(id+"F5.boolean.opBoolean","SPLIT",FACE,{"disambiguationData":[TD([makeQuery(id+"F5.opExtrude","SWEPT_FACE",FACE,{"disambiguationData":[OSD([sQuery(id+"F4.wireOp",EDGE,"E41")])]})])],"derivedFrom":makeQuery(id+"F3.boolean.opBoolean","COPY",FACE,{"derivedFrom":makeQuery(id+"F3.opExtrude","CAP_FACE",FACE,{"disambiguationData":[OSD([sQuery(id+"F0.wireOp",EDGE,"E25.0"),sQuery(id+"F0.wireOp",EDGE,"E25.1"),sQuery(id+"F0.wireOp",EDGE,"E25.2"),sQuery(id+"F0.wireOp",EDGE,"E25.3"),sQuery(id+"F0.wireOp",EDGE,"E25.4"),sQuery(id+"F0.wireOp",EDGE,"E25.5"),sQuery(id+"F0.wireOp",EDGE,"E25.6"),sQuery(id+"F0.wireOp",EDGE,"E25.7")])],"isStart":false})})});
            extrude(context, id + "F13", {"entities" : qUnion([Q0]), "operationType" : NewBodyOperationType.REMOVE, "endBound" : BoundingType.UP_TO_SURFACE, "endBoundEntityFace" : qUnion([Q1]), "depth" : 25 * mm});
        }
        {
            var Q0;
            Q0=makeQuery(id+"F3.boolean.opBoolean","COPY",EDGE,{"derivedFrom":makeQuery(id+"F3.opExtrude","CAP_EDGE",EDGE,{"disambiguationData":[OSD([sQuery(id+"F0.wireOp",EDGE,"E25.6")])],"isStart":false})});
            var Q1;
            Q1=makeQuery(id+"F8.boolean.opBoolean","INTERSECT",EDGE,{"derivedFrom":[makeQuery(id+"F5.opExtrude","SWEPT_FACE",FACE,{"disambiguationData":[OSD([sQuery(id+"F4.wireOp",EDGE,"E30")])]}),makeQuery(id+"F8.opExtrude","CAP_FACE",FACE,{"disambiguationData":[OSD([sQuery(id+"F7.wireOp",EDGE,"E67")])],"isStart":false})]});
            var Q2;
            Q2=makeQuery(id+"F8.boolean.opBoolean","INTERSECT",EDGE,{"disambiguationData":[OD(1.0)],"derivedFrom":[makeQuery(id+"F5.opExtrude","SWEPT_FACE",FACE,{"disambiguationData":[OSD([sQuery(id+"F4.wireOp",EDGE,"E30")])]}),makeQuery(id+"F8.opExtrude","SWEPT_FACE",FACE,{"disambiguationData":[OSD([sQuery(id+"F7.wireOp",EDGE,"E67")])]})]});
            var Q3;
            {var subQ0=makeQuery(id+"F3.boolean.opBoolean","COPY",FACE,{"derivedFrom":makeQuery(id+"F3.opExtrude","CAP_FACE",FACE,{"disambiguationData":[OSD([sQuery(id+"F0.wireOp",EDGE,"E25.0"),sQuery(id+"F0.wireOp",EDGE,"E25.1"),sQuery(id+"F0.wireOp",EDGE,"E25.2"),sQuery(id+"F0.wireOp",EDGE,"E25.3"),sQuery(id+"F0.wireOp",EDGE,"E25.4"),sQuery(id+"F0.wireOp",EDGE,"E25.5"),sQuery(id+"F0.wireOp",EDGE,"E25.6"),sQuery(id+"F0.wireOp",EDGE,"E25.7")])],"isStart":false})});var subQ1=sQuery(id+"F4.wireOp",EDGE,"E30");Q3=makeQuery(id+"F8.boolean.opBoolean","SPLIT",EDGE,{"disambiguationData":[TD([makeQuery(id+"F5.opExtrude","SWEPT_FACE",FACE,{"disambiguationData":[OSD([sQuery(id+"F4.wireOp",EDGE,"E35.filletArc")])]})])],"derivedFrom":makeQuery(id+"F5.opExtrude","TWEAK_EDGE",EDGE,{"derivedFrom":[subQ0,makeQuery(id+"F4.imprint","IMPRINT",EDGE,{"derivedFrom":subQ1})]})});}
            var Q4;
            {var subQ0=sQuery(id+"F0.wireOp",EDGE,"E25.0");var subQ1=sQuery(id+"F0.wireOp",EDGE,"E25.1");var subQ2=sQuery(id+"F0.wireOp",EDGE,"E25.2");var subQ3=sQuery(id+"F0.wireOp",EDGE,"E25.3");var subQ4=sQuery(id+"F0.wireOp",EDGE,"E25.4");var subQ5=sQuery(id+"F0.wireOp",EDGE,"E25.5");var subQ6=sQuery(id+"F0.wireOp",EDGE,"E25.6");var subQ7=sQuery(id+"F0.wireOp",EDGE,"E25.7");Q4=makeQuery(id+"F8.boolean.opBoolean","INTERSECT",EDGE,{"derivedFrom":[makeQuery(id+"F5.boolean.opBoolean","SPLIT",FACE,{"disambiguationData":[TD([makeQuery(id+"F2.opExtrude","SWEPT_FACE",FACE,{"disambiguationData":[OSD([subQ0])]})])],"derivedFrom":makeQuery(id+"F3.boolean.opBoolean","COPY",FACE,{"derivedFrom":makeQuery(id+"F3.opExtrude","CAP_FACE",FACE,{"disambiguationData":[OSD([subQ0,subQ1,subQ2,subQ3,subQ4,subQ5,subQ6,subQ7])],"isStart":false})})}),makeQuery(id+"F8.opExtrude","SWEPT_FACE",FACE,{"disambiguationData":[OSD([sQuery(id+"F7.wireOp",EDGE,"E67")])]})]});}
            var Q5;
            Q5=makeQuery(id+"F8.boolean.opBoolean","INTERSECT",EDGE,{"disambiguationData":[OD(0.0)],"derivedFrom":[makeQuery(id+"F5.opExtrude","SWEPT_FACE",FACE,{"disambiguationData":[OSD([sQuery(id+"F4.wireOp",EDGE,"E30")])]}),makeQuery(id+"F8.opExtrude","SWEPT_FACE",FACE,{"disambiguationData":[OSD([sQuery(id+"F7.wireOp",EDGE,"E67")])]})]});
            fillet(context, id + "F14", {"entities" : qUnion([Q0, Q1, Q2, Q3, Q4, Q5]), "radius" : 3 * mm, "tangentPropagation" : true, "allowEdgeOverflow" : false});
        }
        {
            var Q0;
            Q0=makeQuery(id+"F1.opExtrude","CAP_EDGE",EDGE,{"disambiguationData":[OSD([sQuery(id+"F0.wireOp",EDGE,"E1.bottom")])],"isStart":false});
            fillet(context, id + "F15", {"entities" : qUnion([Q0]), "radius" : 2 * mm, "tangentPropagation" : true, "allowEdgeOverflow" : false});
        }
        {
            var Q0;
            Q0=qCreatedBy(makeId("Top.planeOp"),FACE);
            var sketch = newSketch(context, id + "F16", { "sketchPlane" : qUnion([Q0])});
            skCircle(sketch, "E79.0", {"center": v(-60, 53.33) * mm, "radius": 4 * mm});
            skCircle(sketch, "E79.1", {"center": v(60, 53.33) * mm, "radius": 4 * mm});
            skCircle(sketch, "E79.2", {"center": v(60, -53.33) * mm, "radius": 4 * mm});
            skCircle(sketch, "E79.3", {"center": v(-60, -53.33) * mm, "radius": 4 * mm});
            skArc(sketch, "E79.4", {"start": v(-52.38, -47.01) * mm, "mid": v(0, -53.33) * mm, "end": v(52.38, -47.01) * mm});
            skArc(sketch, "E79.5", {"start": v(-60, -37.3) * mm, "mid": v(-57.87, -43.47) * mm, "end": v(-52.38, -47.01) * mm});
            skLineSegment(sketch, "E79.6", {"start": v(-60, 37.3) * mm, "end": v(-60, -37.3) * mm});
            skArc(sketch, "E79.7", {"start": v(-52.38, 47.01) * mm, "mid": v(-57.87, 43.47) * mm, "end": v(-60, 37.3) * mm});
            skArc(sketch, "E79.8", {"start": v(52.38, 47.01) * mm, "mid": v(0, 53.33) * mm, "end": v(-52.38, 47.01) * mm});
            skArc(sketch, "E79.9", {"start": v(60, 37.3) * mm, "mid": v(57.87, 43.47) * mm, "end": v(52.38, 47.01) * mm});
            skLineSegment(sketch, "E79.10", {"start": v(60, 37.3) * mm, "end": v(60, -37.3) * mm});
            skArc(sketch, "E79.11", {"start": v(52.38, -47.01) * mm, "mid": v(57.87, -43.47) * mm, "end": v(60, -37.3) * mm});
            skLineSegment(sketch, "E79.12", {"start": v(90, -70) * mm, "end": v(90, 70) * mm});
            skArc(sketch, "E79.13", {"start": v(80, -80) * mm, "mid": v(87.07, -77.07) * mm, "end": v(90, -70) * mm});
            skLineSegment(sketch, "E79.14", {"start": v(-80, -80) * mm, "end": v(80, -80) * mm});
            skArc(sketch, "E79.15", {"start": v(-90, -70) * mm, "mid": v(-87.07, -77.07) * mm, "end": v(-80, -80) * mm});
            skLineSegment(sketch, "E79.16", {"start": v(-90, -70) * mm, "end": v(-90, 70) * mm});
            skArc(sketch, "E79.17", {"start": v(-80, 80) * mm, "mid": v(-87.07, 77.07) * mm, "end": v(-90, 70) * mm});
            skLineSegment(sketch, "E79.18", {"start": v(-80, 80) * mm, "end": v(80, 80) * mm});
            skArc(sketch, "E79.19", {"start": v(90, 70) * mm, "mid": v(87.07, 77.07) * mm, "end": v(80, 80) * mm});
            skLineSegment(sketch, "E80", {"start": v(0, 80) * mm, "end": v(0, 110) * mm, "construction": true});
            skPoint(sketch, "E80.endSnap0", {"position": v(0, 80) * mm});
            skLineSegment(sketch, "E81", {"start": v(-15, 110) * mm, "end": v(-15, 98) * mm});
            skLineSegment(sketch, "E82", {"start": v(-15, 98) * mm, "end": v(-33, 80) * mm});
            skLineSegment(sketch, "E83", {"start": v(15, 110) * mm, "end": v(15, 92.25) * mm});
            skLineSegment(sketch, "E84", {"start": v(15, 92.25) * mm, "end": v(27.25, 80) * mm});
            skCircle(sketch, "E85", {"center": v(0, 110) * mm, "radius": 6 * mm});
            skArc(sketch, "E86", {"start": v(15, 110) * mm, "mid": v(0, 125) * mm, "end": v(-15, 110) * mm});
            skLineSegment(sketch, "E87", {"start": v(-90, 0) * mm, "end": v(90, 0) * mm, "construction": true});
            skLineSegment(sketch, "E88.MirrorCS", {"start": v(-15, -98) * mm, "end": v(-33, -80) * mm});
            skLineSegment(sketch, "E89.MirrorCS", {"start": v(-15, -110) * mm, "end": v(-15, -98) * mm});
            skArc(sketch, "E90.MirrorCS", {"start": v(15, -110) * mm, "mid": v(0, -125) * mm, "end": v(-15, -110) * mm});
            skLineSegment(sketch, "E91.MirrorCS", {"start": v(15, -92.25) * mm, "end": v(27.25, -80) * mm});
            skLineSegment(sketch, "E92.MirrorCS", {"start": v(15, -110) * mm, "end": v(15, -92.25) * mm});
            skCircle(sketch, "E93.MirrorC", {"center": v(0, -110) * mm, "radius": 6 * mm});
            skLineSegment(sketch, "E94.MirrorCS", {"start": v(0, -80) * mm, "end": v(0, -110) * mm, "construction": true});
            skSolve(sketch);
        }
        {
            var Q0;
            Q0=makeQuery(id+"F16.imprint","IMPRINT",FACE,{"disambiguationData":[TD([[makeQuery(id+"F16.imprint","IMPRINT",EDGE,{"derivedFrom":sQuery(id+"F16.wireOp",EDGE,"E79.0")}),-1.0]])]});
            var Q1;
            {var subQ0=sQuery(id+"F16.wireOp",EDGE,"E88.MirrorCS");Q1=makeQuery(id+"F16.imprint","IMPRINT",FACE,{"disambiguationData":[TD([[makeQuery(id+"F16.imprint","IMPRINT",EDGE,{"derivedFrom":subQ0}),-1.0]])]});}
            var Q2;
            Q2=makeQuery(id+"F16.imprint","IMPRINT",FACE,{"disambiguationData":[TD([[makeQuery(id+"F16.imprint","IMPRINT",EDGE,{"derivedFrom":sQuery(id+"F16.wireOp",EDGE,"E81")}),1.0]])]});
            var Q3;
            Q3=makeQuery(id+"F2.opExtrude","CAP_FACE",FACE,{"disambiguationData":[OSD([sQuery(id+"F0.wireOp",EDGE,"E12"),sQuery(id+"F0.wireOp",EDGE,"E13"),sQuery(id+"F0.wireOp",EDGE,"E14"),sQuery(id+"F0.wireOp",EDGE,"E15"),sQuery(id+"F0.wireOp",EDGE,"E17.filletArc"),sQuery(id+"F0.wireOp",EDGE,"E18.filletArc"),sQuery(id+"F0.wireOp",EDGE,"E19.filletArc"),sQuery(id+"F0.wireOp",EDGE,"E20.filletArc"),sQuery(id+"F0.wireOp",EDGE,"E25.0"),sQuery(id+"F0.wireOp",EDGE,"E25.1"),sQuery(id+"F0.wireOp",EDGE,"E25.2"),sQuery(id+"F0.wireOp",EDGE,"E25.3"),sQuery(id+"F0.wireOp",EDGE,"E25.4"),sQuery(id+"F0.wireOp",EDGE,"E25.5"),sQuery(id+"F0.wireOp",EDGE,"E25.6"),sQuery(id+"F0.wireOp",EDGE,"E25.7")])],"isStart":false});
            extrude(context, id + "F17", {"entities" : qUnion([Q0, Q1, Q2]), "operationType" : NewBodyOperationType.ADD, "endBound" : BoundingType.UP_TO_SURFACE, "endBoundEntityFace" : qUnion([Q3]), "depth" : 25 * mm});
        }
    });
